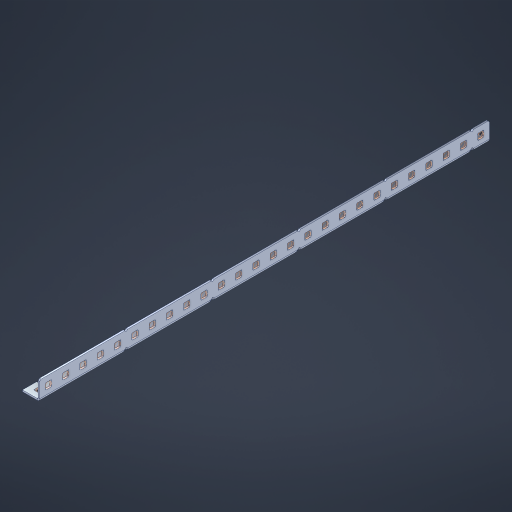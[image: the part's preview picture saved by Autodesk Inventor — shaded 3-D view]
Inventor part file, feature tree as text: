
AUTODESK INVENTOR PART (.ipt)
format: ipt  version: 2023 (Build 270158000, 158)  size: 1,116,160 bytes
history: native  units: in
note: dims shown in document units (in); Inventor stores cm internally (conversion verified against a paired STEP export)
features: other x85, extrude x76, sheet_metal_op x11, sketch x10, pattern_linear x2, mirror x1, chamfer x1
ambient origin geometry x8: Origin, YZ Plane, XZ Plane, XY Plane, X Axis, Y Axis, Z Axis, Center Point
bodies: Solid1 (feature_tree), Body (feature_tree)
feature tree (186):
  sheet_metal_op  "Flanges"
  other  "Flange Pattern Plane"
  other  "Flange Pattern Sketch"
  sheet_metal_op  "Flange Pattern"
  sheet_metal_op  "Body Pattern"
  pattern_linear  "Center Pattern"  Spacing1=0.0469in  [1 undecoded]
  other  "Arc Length"
  mirror  "Notch Mirror"
  pattern_linear  "Notch Pattern"  Spacing1=0.182in  [1 undecoded]
  chamfer  "End Chamfer"
  extrude  "Half Cut"  Depth=0.02in
  sketch  "Sketch1"  dims[d0=1.0in]
  other  "Plate1"
  sketch  "Sketch2"  dims[d1=13.0in]
  other  "Plate2"
  sheet_metal_op  "Bend1"
  sheet_metal_op  "Corner1"
  sketch  "Sketch3"  dims[d2=0.0469in]
  sketch  "Sketch7"  dims[d3=0.0469in]
  other  "Srf1"
  other  "Srf2"
  sketch  "Sketch8"  dims[d4=0.0234in]
  sketch  "Sketch9"  dims[d5=0.0938in]
  other  "Srf91"
  sheet_metal_op  "Body Pattern Sketch"
  other  "Srf92"
  sketch  "Sketch13"  dims[d6=0.0469in]
  sketch  "Sketch14"  dims[d7=0.5in d8=90.0deg d9=0.0312in]
  sketch  "Sketch15"  dims[d10=0.1875in]
  sketch  "Sketch16"  dims[d11=0.0469in d12=0.0469in d16=0.182in d17=0.02in d18=0.0469in d19=0.0in d20=0.25in d21=0.25in d38=10.2362in d40=0.5in d41=0.3937in d43=1.0in d46=0.172in d47=1.0in d48=0.0in d49=0.182in d50=0.02in d51=0.25in d52=0.25in d53=0.0469in d54=0.0in d55=0.172in d56=1.0in d57=0.0in d58=0.25in d60=10.2362in d62=0.5in d63=0.3937in d65=0.5in d85=0.1227in d86=0.1659in d88=0.04in d89=0.0469in d90=0.0in d91=0.04in d92=0.0491in d95=2.5in d96=0.04in d97=0.25in d98=45.0deg d99=0.25in d100=0.5in d101=0.0in d102=2.497in d106=0.182in d107=0.02in d108=0.5in d109=0.5in d110=0.0469in d111=0.0in d112=0.172in d113=0.5in d114=0.0in d117=0.5in d118=0.5in d119=0.5in]
  other  "Srf786"
  other  "Srf823"
  other  "Srf824"
  other  "Srf825"
  other  "Srf826"
  other  "Srf827"
  other  "Srf828"
  other  "Srf829"
  other  "Srf856"
  other  "Srf857"
  other  "Srf858"
  other  "Srf859"
  other  "Srf860"
  other  "Srf861"
  other  "Srf862"
  other  "Srf889"
  other  "Srf890"
  other  "Srf891"
  other  "Srf892"
  other  "Srf893"
  other  "Srf894"
  other  "Srf895"
  other  "Srf896"
  other  "Srf922"
  other  "Srf923"
  other  "Srf924"
  other  "Srf925"
  other  "Srf926"
  other  "Srf959"
  other  "Srf960"
  other  "Srf961"
  other  "Srf962"
  other  "Srf963"
  other  "Srf996"
  other  "Srf997"
  other  "Srf998"
  other  "Srf999"
  other  "Srf1000"
  other  "Srf1143"
  other  "Srf1144"
  other  "Srf1145"
  other  "Srf1146"
  other  "Srf1147"
  other  "Srf1148"
  other  "Srf1149"
  other  "Srf1150"
  other  "Srf1151"
  other  "Srf1152"
  other  "Srf1153"
  other  "Srf1154"
  other  "Srf1199"
  other  "Srf1200"
  other  "Srf1201"
  other  "Srf1202"
  other  "Srf1203"
  other  "Srf1204"
  other  "Srf1205"
  other  "Srf1206"
  other  "Srf1207"
  other  "Srf1208"
  other  "Srf1209"
  other  "Srf1210"
  other  "Srf1255"
  other  "Srf1256"
  other  "Srf1257"
  other  "Srf1258"
  other  "Srf1259"
  other  "Srf1260"
  other  "Srf1261"
  other  "Srf1262"
  other  "Srf1263"
  other  "Srf1264"
  other  "Srf1265"
  other  "Srf1266"
  sheet_metal_op  "Flange Stamp"
  sheet_metal_op  "Flange Circle"
  sheet_metal_op  "Body Stamp"
  sheet_metal_op  "Body Circle"
  other  "Center Stamp"
  other  "Center Circle"
  sheet_metal_op  "Notch"
  extrude  "ExtrusionSrf2"  Depth=0.0469in
  extrude  "ExtrusionSrf92"  TaperAngle=0.0deg  [1 undecoded]
  extrude  "ExtrusionSrf823"  Depth=0.25in
  extrude  "ExtrusionSrf824"  Depth=0.25in
  extrude  "ExtrusionSrf825"  Depth=0.5in
  extrude  "ExtrusionSrf826"  Depth=0.5in
  extrude  "ExtrusionSrf827"  Depth=1.0in TaperAngle=0.0deg
  extrude  "ExtrusionSrf828"  Depth=0.182in
  extrude  "ExtrusionSrf829"  Depth=0.02in
  extrude  "ExtrusionSrf856"  Depth=0.25in
  extrude  "ExtrusionSrf857"  Depth=0.25in
  extrude  "ExtrusionSrf858"  Depth=0.0469in
  extrude  "ExtrusionSrf859"  TaperAngle=0.0deg  [1 undecoded]
  extrude  "ExtrusionSrf860"  Depth=0.5in
  extrude  "ExtrusionSrf861"  Depth=1.0in TaperAngle=0.0deg
  extrude  "ExtrusionSrf862"  Depth=0.25in
  extrude  "ExtrusionSrf889"  Depth=0.5in
  extrude  "ExtrusionSrf890"  Depth=0.5in
  extrude  "ExtrusionSrf891"  Depth=0.5in
  extrude  "ExtrusionSrf892"  Depth=0.5in
  extrude  "ExtrusionSrf893"  Depth=0.5in
  extrude  "ExtrusionSrf894"  Depth=0.0469in
  extrude  "ExtrusionSrf895"  TaperAngle=0.0deg  [1 undecoded]
  extrude  "ExtrusionSrf896"  Depth=0.5in
  extrude  "ExtrusionSrf922"  Depth=0.5in
  extrude  "ExtrusionSrf923"  Depth=2.5in
  extrude  "ExtrusionSrf924"  Depth=0.25in TaperAngle=45.0deg
  extrude  "ExtrusionSrf925"  Depth=0.25in
  extrude  "ExtrusionSrf926"  Depth=0.5in TaperAngle=0.0deg
  extrude  "ExtrusionSrf959"  Depth=0.5in
  extrude  "ExtrusionSrf960"  Depth=0.182in
  extrude  "ExtrusionSrf961"  Depth=0.02in
  extrude  "ExtrusionSrf962"  Depth=0.5in
  extrude  "ExtrusionSrf963"  Depth=0.5in
  extrude  "ExtrusionSrf996"  Depth=0.0469in
  extrude  "ExtrusionSrf997"  TaperAngle=0.0deg  [1 undecoded]
  extrude  "ExtrusionSrf998"  Depth=0.5in
  extrude  "ExtrusionSrf999"  Depth=0.5in TaperAngle=0.0deg
  extrude  "ExtrusionSrf1000"  Depth=0.5in
  extrude  "ExtrusionSrf1143"  Depth=0.5in
  extrude  "ExtrusionSrf1144"  Depth=0.5in
  extrude  "ExtrusionSrf1145"  [1 undecoded]
  extrude  "ExtrusionSrf1146"  [1 undecoded]
  extrude  "ExtrusionSrf1147"  [1 undecoded]
  extrude  "ExtrusionSrf1148"  [1 undecoded]
  extrude  "ExtrusionSrf1149"  [1 undecoded]
  extrude  "ExtrusionSrf1150"  [1 undecoded]
  extrude  "ExtrusionSrf1151"  [1 undecoded]
  extrude  "ExtrusionSrf1152"  [1 undecoded]
  extrude  "ExtrusionSrf1153"  [1 undecoded]
  extrude  "ExtrusionSrf1154"  [1 undecoded]
  extrude  "ExtrusionSrf1199"  [1 undecoded]
  extrude  "ExtrusionSrf1200"  [1 undecoded]
  extrude  "ExtrusionSrf1201"  [1 undecoded]
  extrude  "ExtrusionSrf1202"  [1 undecoded]
  extrude  "ExtrusionSrf1203"  [1 undecoded]
  extrude  "ExtrusionSrf1204"  [1 undecoded]
  extrude  "ExtrusionSrf1205"  [1 undecoded]
  extrude  "ExtrusionSrf1206"  [1 undecoded]
  extrude  "ExtrusionSrf1207"  [1 undecoded]
  extrude  "ExtrusionSrf1208"  [1 undecoded]
  extrude  "ExtrusionSrf1209"  [1 undecoded]
  extrude  "ExtrusionSrf1210"  [1 undecoded]
  extrude  "ExtrusionSrf1255"  [1 undecoded]
  extrude  "ExtrusionSrf1256"  [1 undecoded]
  extrude  "ExtrusionSrf1257"  [1 undecoded]
  extrude  "ExtrusionSrf1258"  [1 undecoded]
  extrude  "ExtrusionSrf1259"  [1 undecoded]
  extrude  "ExtrusionSrf1260"  [1 undecoded]
  extrude  "ExtrusionSrf1261"  [1 undecoded]
  extrude  "ExtrusionSrf1262"  [1 undecoded]
  extrude  "ExtrusionSrf1263"  [1 undecoded]
  extrude  "ExtrusionSrf1264"  [1 undecoded]
  extrude  "ExtrusionSrf1265"  [1 undecoded]
  extrude  "ExtrusionSrf1266"  [1 undecoded]
note: 40 required parameter values undecoded (feature->parameter linkage not recoverable at this tier; creation-order binding heuristic only, values carry confidence <= 0.55)
